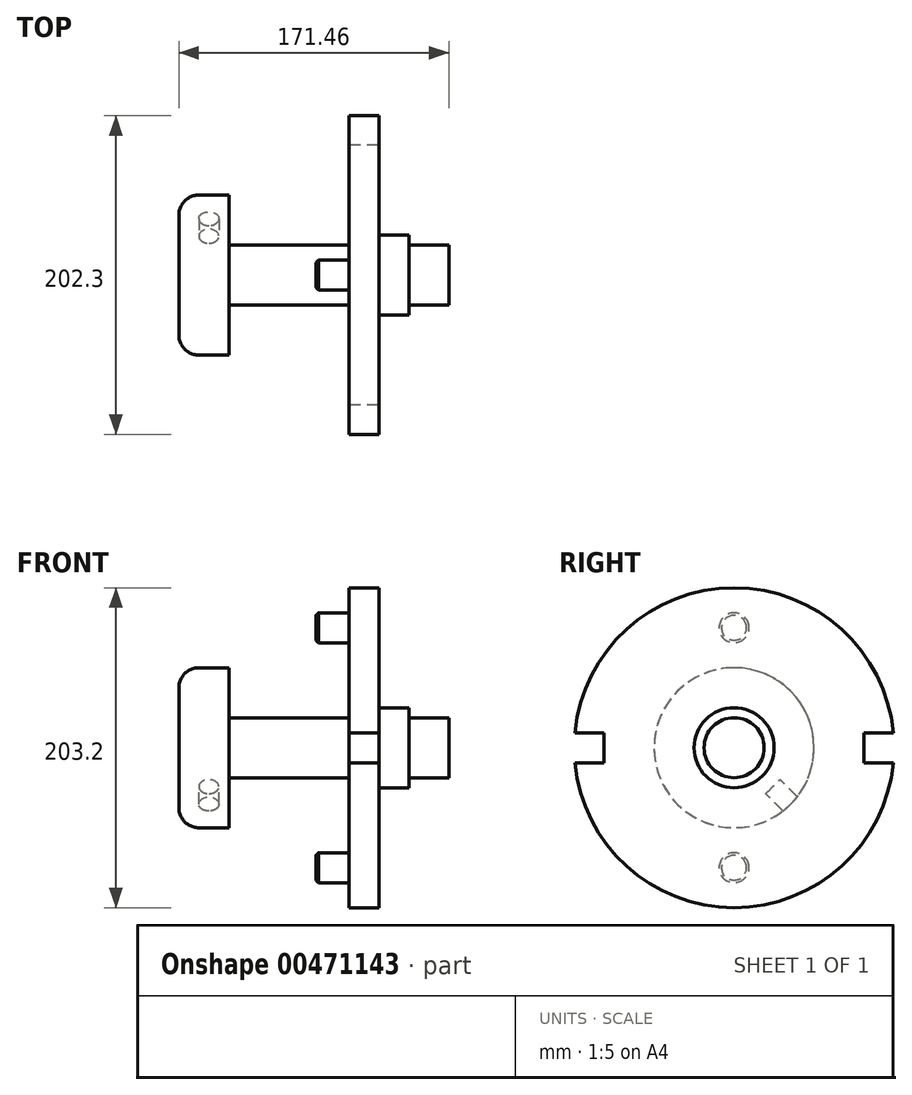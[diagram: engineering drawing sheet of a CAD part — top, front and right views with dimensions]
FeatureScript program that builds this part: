
annotation { "Feature Type Name" : "Feature", "Feature Type Description" : "" }
export const myFeature = defineFeature(function(context is Context, id is Id, definition is map)
    precondition{}
    {
        {
            var Q0;
            Q0=qCreatedBy(makeId("Top.planeOp"),FACE);
            var sketch = newSketch(context, id + "F0", { "sketchPlane" : qUnion([Q0])});
            skLineSegment(sketch, "E0", {"start": v(-85.72, 0) * mm, "end": v(85.72, 0) * mm});
            skLineSegment(sketch, "E1", {"start": v(-85.73, 0) * mm, "end": v(-85.73, 38.1) * mm});
            skLineSegment(sketch, "E2", {"start": v(-73.03, 50.8) * mm, "end": v(-53.98, 50.8) * mm});
            skLineSegment(sketch, "E3", {"start": v(-53.98, 50.8) * mm, "end": v(-53.98, 19.05) * mm});
            skLineSegment(sketch, "E4", {"start": v(-53.98, 19.05) * mm, "end": v(22.22, 19.05) * mm});
            skLineSegment(sketch, "E5", {"start": v(22.22, 19.05) * mm, "end": v(22.22, 101.6) * mm});
            skLineSegment(sketch, "E6", {"start": v(22.22, 101.6) * mm, "end": v(41.27, 101.6) * mm});
            skLineSegment(sketch, "E7", {"start": v(41.27, 101.6) * mm, "end": v(41.27, 25.4) * mm});
            skLineSegment(sketch, "E8", {"start": v(41.27, 25.4) * mm, "end": v(60.32, 25.4) * mm});
            skLineSegment(sketch, "E9", {"start": v(60.32, 25.4) * mm, "end": v(60.32, 19.05) * mm});
            skLineSegment(sketch, "E10", {"start": v(60.32, 19.05) * mm, "end": v(85.73, 19.05) * mm});
            skLineSegment(sketch, "E11", {"start": v(85.73, 19.05) * mm, "end": v(85.73, 0) * mm});
            skPoint(sketch, "E12.visualSharp", {"position": v(-85.73, 50.8) * mm});
            skArc(sketch, "E12.filletArc", {"start": v(-73.03, 50.8) * mm, "mid": v(-82, 47.08) * mm, "end": v(-85.73, 38.1) * mm});
            skSolve(sketch);
        }
        {
            var Q0;
            Q0=makeQuery(id+"F0.imprint","IMPRINT",FACE,{"disambiguationData":[TD([[makeQuery(id+"F0.imprint","IMPRINT",EDGE,{"derivedFrom":sQuery(id+"F0.wireOp",EDGE,"E0")}),1.0]])]});
            var Q1;
            Q1=sQuery(id+"F0.wireOp",EDGE,"E0");
            revolve(context, id + "F1", {"entities" : qUnion([Q0]), "axis" : qUnion([Q1]), "revolveType" : RevolveType.FULL});
        }
        {
            var Q0;
            Q0=makeQuery(id+"F1.opRevolve","SWEPT_FACE",FACE,{"disambiguationData":[OSD([sQuery(id+"F0.wireOp",EDGE,"E5")])]});
            var sketch = newSketch(context, id + "F2", { "sketchPlane" : qUnion([Q0])});
            skCircle(sketch, "E13.0.0", {"center": v(0, 0) * mm, "radius": 101.6 * mm});
            skLineSegment(sketch, "E14.bottom", {"start": v(-82.55, -9.53) * mm, "end": v(-107.95, -9.53) * mm});
            skLineSegment(sketch, "E14.top", {"start": v(-82.55, 9.53) * mm, "end": v(-107.95, 9.53) * mm});
            skLineSegment(sketch, "E14.left", {"start": v(-82.55, -9.53) * mm, "end": v(-82.55, 9.53) * mm});
            skLineSegment(sketch, "E14.right", {"start": v(-107.95, -9.53) * mm, "end": v(-107.95, 9.52) * mm});
            skLineSegment(sketch, "E15.bottom", {"start": v(82.55, 9.53) * mm, "end": v(107.95, 9.53) * mm});
            skLineSegment(sketch, "E15.top", {"start": v(82.55, -9.52) * mm, "end": v(107.95, -9.52) * mm});
            skLineSegment(sketch, "E15.left", {"start": v(82.55, 9.53) * mm, "end": v(82.55, -9.52) * mm});
            skLineSegment(sketch, "E15.right", {"start": v(107.95, 9.53) * mm, "end": v(107.95, -9.52) * mm});
            skSolve(sketch);
        }
        {
            var Q0;
            {var subQ5=sQuery(id+"F2.wireOp",EDGE,"E14.right");Q0=makeQuery(id+"F2.imprint","IMPRINT",FACE,{"disambiguationData":[TD([[makeQuery(id+"F2.imprint","IMPRINT",EDGE,{"derivedFrom":subQ5}),-1.0]])]});}
            var Q1;
            {var subQ5=sQuery(id+"F2.wireOp",EDGE,"E15.right");Q1=makeQuery(id+"F2.imprint","IMPRINT",FACE,{"disambiguationData":[TD([[makeQuery(id+"F2.imprint","IMPRINT",EDGE,{"derivedFrom":subQ5}),-1.0]])]});}
            var Q2;
            {var subQ5=sQuery(id+"F2.wireOp",EDGE,"E15.left");Q2=makeQuery(id+"F2.imprint","IMPRINT",FACE,{"disambiguationData":[TD([[makeQuery(id+"F2.imprint","IMPRINT",EDGE,{"derivedFrom":subQ5}),1.0]])]});}
            var Q3;
            {var subQ5=sQuery(id+"F2.wireOp",EDGE,"E14.left");Q3=makeQuery(id+"F2.imprint","IMPRINT",FACE,{"disambiguationData":[TD([[makeQuery(id+"F2.imprint","IMPRINT",EDGE,{"derivedFrom":subQ5}),1.0]])]});}
            extrude(context, id + "F3", {"entities" : qUnion([Q0, Q1, Q2, Q3]), "operationType" : NewBodyOperationType.REMOVE, "oppositeDirection" : true, "depth" : 25.4 * mm});
        }
        {
            var Q0;
            Q0=makeQuery(id+"F1.opRevolve","SWEPT_FACE",FACE,{"disambiguationData":[OSD([sQuery(id+"F0.wireOp",EDGE,"E5")])]});
            var sketch = newSketch(context, id + "F4", { "sketchPlane" : qUnion([Q0])});
            skCircle(sketch, "E16", {"center": v(0, 76.2) * mm, "radius": 9.53 * mm});
            skCircle(sketch, "E17", {"center": v(0, -76.2) * mm, "radius": 9.53 * mm});
            skSolve(sketch);
        }
        {
            var Q0;
            Q0=makeQuery(id+"F4.imprint","IMPRINT",FACE,{"disambiguationData":[TD([[makeQuery(id+"F4.imprint","IMPRINT",EDGE,{"derivedFrom":sQuery(id+"F4.wireOp",EDGE,"E16")}),1.0]])]});
            var Q1;
            Q1=makeQuery(id+"F4.imprint","IMPRINT",FACE,{"disambiguationData":[TD([[makeQuery(id+"F4.imprint","IMPRINT",EDGE,{"derivedFrom":sQuery(id+"F4.wireOp",EDGE,"E17")}),1.0]])]});
            extrude(context, id + "F5", {"entities" : qUnion([Q0, Q1]), "operationType" : NewBodyOperationType.ADD, "depth" : 20.83 * mm});
        }
        {
            var Q0;
            Q0=makeQuery(id+"F5.opExtrude","CAP_EDGE",EDGE,{"disambiguationData":[OSD([sQuery(id+"F4.wireOp",EDGE,"E16")])],"isStart":false});
            var Q1;
            Q1=makeQuery(id+"F5.opExtrude","CAP_EDGE",EDGE,{"disambiguationData":[OSD([sQuery(id+"F4.wireOp",EDGE,"E17")])],"isStart":false});
            chamfer(context, id + "F6", {"entities" : qUnion([Q0, Q1]), "width" : 1.59 * mm, "tangentPropagation" : true});
        }
        {
            var Q0;
            Q0=makeQuery(id+"F1.opRevolve","SWEPT_FACE",FACE,{"disambiguationData":[OSD([sQuery(id+"F0.wireOp",EDGE,"E3")])]});
            cPlane(context, id + "F7", {"entities" : qUnion([Q0]), "cplaneType" : CPlaneType.OFFSET, "offset" : 12.7 * mm, "oppositeDirection" : true, "width" : 152.4 * mm, "height" : 152.4 * mm});
        }
        {
            var Q0;
            Q0=qCreatedBy(id+"F7.planeOp",FACE);
            var sketch = newSketch(context, id + "F8", { "sketchPlane" : qUnion([Q0])});
            skLineSegment(sketch, "E18", {"start": v(0, 0) * mm, "end": v(0, -21.74) * mm});
            skCircle(sketch, "E19.0", {"center": v(0, 0) * mm, "radius": 50.8 * mm, "construction": true});
            skLineSegment(sketch, "E20", {"start": v(35.92, -35.92) * mm, "end": v(24.7, -24.7) * mm});
            skLineSegment(sketch, "E21", {"start": v(24.7, -24.7) * mm, "end": v(29.19, -20.2) * mm});
            skLineSegment(sketch, "E22", {"start": v(29.19, -20.2) * mm, "end": v(44, -35.02) * mm});
            skLineSegment(sketch, "E23", {"start": v(44, -35.02) * mm, "end": v(39.51, -39.51) * mm});
            skLineSegment(sketch, "E24", {"start": v(39.51, -39.51) * mm, "end": v(35.92, -35.92) * mm});
            skLineSegment(sketch, "E25", {"start": v(24.7, -24.7) * mm, "end": v(0, 0) * mm, "construction": true});
            skSolve(sketch);
        }
        {
            var Q0;
            Q0=makeQuery(id+"F8.imprint","IMPRINT",FACE,{"disambiguationData":[TD([[makeQuery(id+"F8.imprint","IMPRINT",EDGE,{"derivedFrom":sQuery(id+"F8.wireOp",EDGE,"E20")}),-1.0]])]});
            var Q1;
            Q1=sQuery(id+"F8.wireOp",EDGE,"E20");
            revolve(context, id + "F9", {"operationType" : NewBodyOperationType.REMOVE, "entities" : qUnion([Q0]), "axis" : qUnion([Q1]), "revolveType" : RevolveType.FULL, "oppositeDirection" : true});
        }
    });
